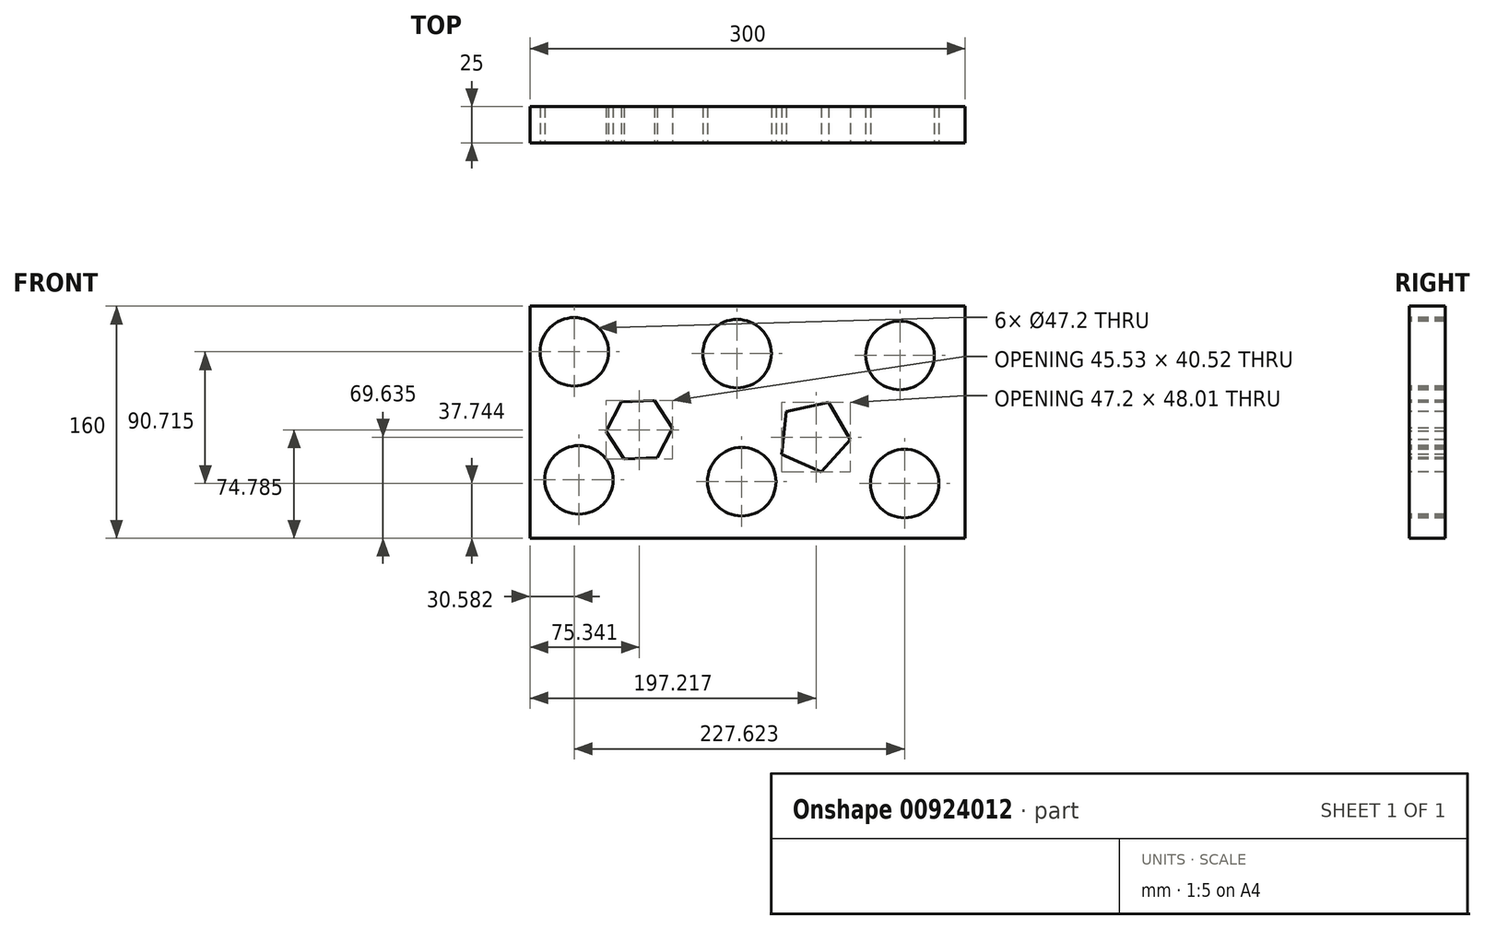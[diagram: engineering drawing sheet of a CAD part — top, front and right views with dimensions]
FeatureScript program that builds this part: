
annotation { "Feature Type Name" : "Feature", "Feature Type Description" : "" }
export const myFeature = defineFeature(function(context is Context, id is Id, definition is map)
    precondition{}
    {
        {
            var Q0;
            Q0=qCreatedBy(makeId("Front.planeOp"),FACE);
            var sketch = newSketch(context, id + "F0", { "sketchPlane" : qUnion([Q0])});
            skLineSegment(sketch, "E0.bottom", {"start": v(-184.8, 39.78) * mm, "end": v(115.2, 39.78) * mm});
            skLineSegment(sketch, "E0.top", {"start": v(-184.8, -120.22) * mm, "end": v(115.2, -120.22) * mm});
            skLineSegment(sketch, "E0.left", {"start": v(-184.8, 39.78) * mm, "end": v(-184.8, -120.22) * mm});
            skLineSegment(sketch, "E0.right", {"start": v(115.2, 39.78) * mm, "end": v(115.2, -120.22) * mm});
            skSolve(sketch);
        }
        {
            var Q0;
            Q0=makeQuery(id+"F0.imprint","IMPRINT",FACE,{"disambiguationData":[TD([[makeQuery(id+"F0.imprint","IMPRINT",EDGE,{"derivedFrom":sQuery(id+"F0.wireOp",EDGE,"E0.bottom")}),-1.0]])]});
            extrude(context, id + "F1", {"entities" : qUnion([Q0]), "depth" : 25 * mm, "offsetDistance" : 25 * mm});
        }
        {
            var Q0;
            Q0=makeQuery(id+"F1.opExtrude","CAP_FACE",FACE,{"disambiguationData":[OSD([sQuery(id+"F0.wireOp",EDGE,"E0.bottom"),sQuery(id+"F0.wireOp",EDGE,"E0.top"),sQuery(id+"F0.wireOp",EDGE,"E0.left"),sQuery(id+"F0.wireOp",EDGE,"E0.right")])],"isStart":false});
            var sketch = newSketch(context, id + "F2", { "sketchPlane" : qUnion([Q0])});
            skCircle(sketch, "E1", {"center": v(-154.2, 8.24) * mm, "radius": 23.6 * mm});
            skCircle(sketch, "E2.0.1.0", {"center": v(-151, -80) * mm, "radius": 23.6 * mm});
            skCircle(sketch, "E2.1.0.0", {"center": v(-42, 7) * mm, "radius": 23.6 * mm});
            skCircle(sketch, "E2.1.1.0", {"center": v(-38.8, -81.24) * mm, "radius": 23.6 * mm});
            skCircle(sketch, "E2.2.0.0", {"center": v(70.2, 5.76) * mm, "radius": 23.6 * mm});
            skCircle(sketch, "E2.2.1.0", {"center": v(73.42, -82.48) * mm, "radius": 23.6 * mm});
            skLineSegment(sketch, "E2.direction1", {"start": v(-154.2, 8.24) * mm, "end": v(-42, 7) * mm, "construction": true});
            skLineSegment(sketch, "E2.direction2", {"start": v(-154.2, 8.24) * mm, "end": v(-151, -80) * mm, "construction": true});
            skSolve(sketch);
        }
        {
            var Q0;
            Q0=makeQuery(id+"F2.imprint","IMPRINT",FACE,{"disambiguationData":[TD([[makeQuery(id+"F2.imprint","IMPRINT",EDGE,{"derivedFrom":sQuery(id+"F2.wireOp",EDGE,"E1")}),1.0]])]});
            var Q1;
            Q1=makeQuery(id+"F2.imprint","IMPRINT",FACE,{"disambiguationData":[TD([[makeQuery(id+"F2.imprint","IMPRINT",EDGE,{"derivedFrom":sQuery(id+"F2.wireOp",EDGE,"E2.1.0.0")}),1.0]])]});
            var Q2;
            Q2=makeQuery(id+"F2.imprint","IMPRINT",FACE,{"disambiguationData":[TD([[makeQuery(id+"F2.imprint","IMPRINT",EDGE,{"derivedFrom":sQuery(id+"F2.wireOp",EDGE,"E2.2.0.0")}),1.0]])]});
            var Q3;
            Q3=makeQuery(id+"F2.imprint","IMPRINT",FACE,{"disambiguationData":[TD([[makeQuery(id+"F2.imprint","IMPRINT",EDGE,{"derivedFrom":sQuery(id+"F2.wireOp",EDGE,"E2.2.1.0")}),1.0]])]});
            var Q4;
            Q4=makeQuery(id+"F2.imprint","IMPRINT",FACE,{"disambiguationData":[TD([[makeQuery(id+"F2.imprint","IMPRINT",EDGE,{"derivedFrom":sQuery(id+"F2.wireOp",EDGE,"E2.1.1.0")}),1.0]])]});
            var Q5;
            Q5=makeQuery(id+"F2.imprint","IMPRINT",FACE,{"disambiguationData":[TD([[makeQuery(id+"F2.imprint","IMPRINT",EDGE,{"derivedFrom":sQuery(id+"F2.wireOp",EDGE,"E2.0.1.0")}),1.0]])]});
            extrude(context, id + "F3", {"entities" : qUnion([Q0, Q1, Q2, Q3, Q4, Q5]), "operationType" : NewBodyOperationType.REMOVE, "endBound" : BoundingType.THROUGH_ALL, "oppositeDirection" : true, "depth" : 25 * mm, "offsetDistance" : 25 * mm});
        }
        {
            var Q0;
            Q0=makeQuery(id+"F1.opExtrude","CAP_FACE",FACE,{"disambiguationData":[OSD([sQuery(id+"F0.wireOp",EDGE,"E0.bottom"),sQuery(id+"F0.wireOp",EDGE,"E0.top"),sQuery(id+"F0.wireOp",EDGE,"E0.left"),sQuery(id+"F0.wireOp",EDGE,"E0.right")])],"isStart":false});
            var sketch = newSketch(context, id + "F4", { "sketchPlane" : qUnion([Q0])});
            skCircle(sketch, "E3.cCircle", {"center": v(-109.45, -45.44) * mm, "radius": 19.74 * mm, "construction": true});
            skLineSegment(sketch, "E3.0", {"start": v(-99.01, -25.17) * mm, "end": v(-86.68, -44.34) * mm});
            skLineSegment(sketch, "E3.1", {"start": v(-86.68, -44.34) * mm, "end": v(-97.12, -64.6) * mm});
            skLineSegment(sketch, "E3.2", {"start": v(-97.12, -64.6) * mm, "end": v(-119.89, -65.7) * mm});
            skLineSegment(sketch, "E3.3", {"start": v(-119.89, -65.7) * mm, "end": v(-132.21, -46.53) * mm});
            skLineSegment(sketch, "E3.4", {"start": v(-132.21, -46.53) * mm, "end": v(-121.78, -26.27) * mm});
            skLineSegment(sketch, "E3.5", {"start": v(-121.78, -26.27) * mm, "end": v(-99.01, -25.17) * mm});
            skPoint(sketch, "E3.0.midPoint", {"position": v(-92.85, -34.76) * mm});
            skSolve(sketch);
        }
        {
            var Q0;
            Q0=makeQuery(id+"F4.imprint","IMPRINT",FACE,{"disambiguationData":[TD([[makeQuery(id+"F4.imprint","IMPRINT",EDGE,{"derivedFrom":sQuery(id+"F4.wireOp",EDGE,"E3.0")}),-1.0]])]});
            extrude(context, id + "F5", {"entities" : qUnion([Q0]), "operationType" : NewBodyOperationType.REMOVE, "endBound" : BoundingType.THROUGH_ALL, "oppositeDirection" : true, "depth" : 25 * mm, "offsetDistance" : 25 * mm});
        }
        {
            var Q0;
            Q0=makeQuery(id+"F1.opExtrude","CAP_FACE",FACE,{"disambiguationData":[OSD([sQuery(id+"F0.wireOp",EDGE,"E0.bottom"),sQuery(id+"F0.wireOp",EDGE,"E0.top"),sQuery(id+"F0.wireOp",EDGE,"E0.left"),sQuery(id+"F0.wireOp",EDGE,"E0.right")])],"isStart":false});
            var sketch = newSketch(context, id + "F6", { "sketchPlane" : qUnion([Q0])});
            skCircle(sketch, "E4.cCircle", {"center": v(10.79, -49.77) * mm, "radius": 20.53 * mm, "construction": true});
            skLineSegment(sketch, "E4.0", {"start": v(21.09, -26.58) * mm, "end": v(36.03, -52.4) * mm});
            skLineSegment(sketch, "E4.1", {"start": v(36.03, -52.4) * mm, "end": v(16.1, -74.59) * mm});
            skLineSegment(sketch, "E4.2", {"start": v(16.1, -74.59) * mm, "end": v(-11.17, -62.48) * mm});
            skLineSegment(sketch, "E4.3", {"start": v(-11.17, -62.48) * mm, "end": v(-8.09, -32.81) * mm});
            skLineSegment(sketch, "E4.4", {"start": v(-8.09, -32.81) * mm, "end": v(21.09, -26.58) * mm});
            skPoint(sketch, "E4.0.midPoint", {"position": v(28.56, -39.5) * mm});
            skSolve(sketch);
        }
        {
            var Q0;
            Q0=makeQuery(id+"F6.imprint","IMPRINT",FACE,{"disambiguationData":[TD([[makeQuery(id+"F6.imprint","IMPRINT",EDGE,{"derivedFrom":sQuery(id+"F6.wireOp",EDGE,"E4.0")}),-1.0]])]});
            extrude(context, id + "F7", {"entities" : qUnion([Q0]), "operationType" : NewBodyOperationType.REMOVE, "endBound" : BoundingType.THROUGH_ALL, "oppositeDirection" : true, "depth" : 25 * mm, "offsetDistance" : 25 * mm});
        }
    });
